# Revit family: 2020751 Feilo Sylvania Lighting Fixtures LYTESPAN 3 3M TRACK WHITE
name_source: partatom
category: Lighting Fixtures
revit_build: Autodesk Revit 2017 (Build: 20190507_1515(x64)
units: mm (PartAtom-declared; Revit-internal decimal feet)

## family parameters
Cut with Voids When Loaded = No
Host = Face
Light Source = No
OmniClass Number = 23.80.70.00
OmniClass Title = Lighting
Part Type = Normal
Room Calculation Point = No
Round Connector Dimension = Use Diameter
Shared = No

## types (1)
- 2020751 LYTESPAN 3 3M TRACK WHITE
    Apparent Load = 0 VA
    Assembly Code = D5020200
    AssetType = Fixed
    ClassificationName = Uniclass2015
    ClassificationValue = EF_70_80
    Color = Aluminium white
    Cost = 0 $
    Default Elevation = 0 mm  [stored 0 ft]
    Description = 3 Circuit Track, compact venturi trunk profile, extruded aluminium body, suitable for surface mounting and suspending, (LxWxH) 3000x37x45mm, 2.75kg, White RAL 9016, Class 1, maximum installed load: 3x3680W (11040W), fuse: 3x16A, supply cable: 5 x 1.5mm², 400 VAC supply
    DocumentationLiterature = http://www.sylvania-lighting.com
    ElectricShockClassification = Class I
    Housing material = White aluminium
    IfcExportAs = IfcLightFixtureType
    IfcExportType = IfcLightFixtureType
    InputVoltage = 240V~
    Keynote = 16500
    Lamp = LED
    Manufacturer = Feilo Sylvania
    ManufacturerName = Feilo Sylvania
    Model = LYTESPAN 3 3M TRACK WHITE
    ModelNumber = 2020751
    ModelReference = LYTESPAN 3 3M TRACK WHITE
    Name = LYTESPAN 3 3M TRACK WHITE
    NominalDepth = 37 mm  [stored 0.121391 ft]
    NominalHeight = 45 mm  [stored 0.147638 ft]
    NominalLength = 3000 mm  [stored 9.84252 ft]
    TransformerRequired = Yes
    Type Image = 2020760.jpg
    TypeName = LYTESPAN 3 3M TRACK WHITE
    URL = http://www.sylvania-lighting.com
    Weight = 3.424 kg
    _BimSpecGuid = 0
    _BimstoreBibleVersion = 15
    _CurrentRevision = 1
    _DistributedBy = //www.feilosylvania.com/en-int/

note: [stored X ft] marks values corroborated as IEEE doubles in the binary element streams (Revit-internal decimal feet)

## geometry (parser evidence)
native form markers: Sweep x3
no freeform markers — native parametric forms only
